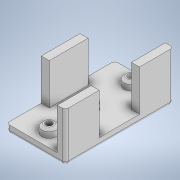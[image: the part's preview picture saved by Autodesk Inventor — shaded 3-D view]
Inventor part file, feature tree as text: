
AUTODESK INVENTOR PART (.ipt)
format: ipt  version: 2020 (Build 240168000, 168)  size: 210,432 bytes
history: native  units: in
note: dims shown in document units (in); Inventor stores cm internally (conversion verified against a paired STEP export)
features: extrude x6, sketch x6, fillet x2, chamfer x1
ambient origin geometry x8: Origin, YZ Plane, XZ Plane, XY Plane, X Axis, Y Axis, Z Axis, Center Point
bodies: Solid1 (feature_tree)
feature tree (15):
  extrude  "Extrusion1"  Depth=2.6378in
  extrude  "Extrusion2"  Depth=0.1969in
  fillet  "Fillet2"  Radius=0.8268in
  extrude  "Extrusion6"  Depth=0.8268in
  fillet  "Fillet3"  Radius=1.0in
  extrude  "Extrusion8"  Depth=0.1969in
  chamfer  "Chamfer1"  Distance=1.0in
  extrude  "Extrusion9"  Depth=0.0197in
  extrude  "Extrusion10"  Depth=0.0197in
  sketch  "Sketch1"  dims[d0=1.4331in d1=2.6378in]
  sketch  "Sketch2"  dims[d2=0.1969in d3=0.0in d4=0.1969in d5=0.8268in]
  sketch  "Sketch6"  dims[d6=0.1969in d7=0.8268in d8=1.0in d9=0.0in]
  sketch  "Sketch8"  dims[d25=0.0787in d26=0.1969in]
  sketch  "Sketch9"  dims[d27=0.9449in d28=1.0in d29=0.0in]
  sketch  "Sketch10"  dims[d36=0.0787in d37=0.3406in d38=0.3406in d39=0.3406in d40=0.1969in d41=0.0in d42=0.0591in d43=0.0787in d44=45.0deg d45=0.1575in d46=0.1575in d47=0.1575in d48=0.7874in d49=0.0in d50=0.2362in d51=0.2362in d52=0.2362in d53=0.0984in d54=0.0in d10=0.0197in d11=0.0344in d13=0.0197in d14=0.0344in d15=0.0197in d16=0.0344in]
